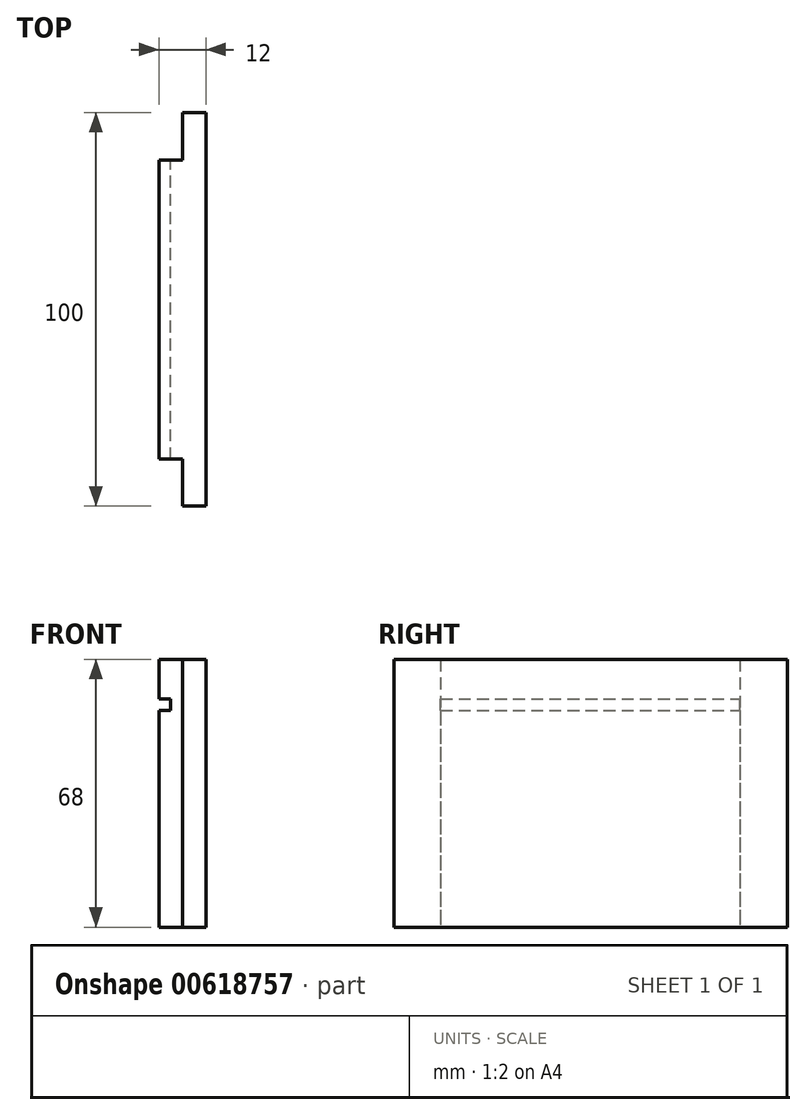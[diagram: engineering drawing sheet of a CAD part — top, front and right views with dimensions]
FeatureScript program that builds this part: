
annotation { "Feature Type Name" : "Feature", "Feature Type Description" : "" }
export const myFeature = defineFeature(function(context is Context, id is Id, definition is map)
    precondition{}
    {
        {
            var Q0;
            Q0=qCreatedBy(makeId("Front.planeOp"),FACE);
            var sketch = newSketch(context, id + "F0", { "sketchPlane" : qUnion([Q0])});
            skLineSegment(sketch, "E0.bottom", {"start": v(6, -34) * mm, "end": v(-6, -34) * mm});
            skLineSegment(sketch, "E0.top", {"start": v(6, 34) * mm, "end": v(-6, 34) * mm});
            skLineSegment(sketch, "E0.left", {"start": v(6, -34) * mm, "end": v(6, 34) * mm});
            skLineSegment(sketch, "E0.right", {"start": v(-6, -34) * mm, "end": v(-6, 21) * mm});
            skPoint(sketch, "E0.middle", {"position": v(0, 0) * mm});
            skLineSegment(sketch, "E1", {"start": v(-6, 34) * mm, "end": v(-6, 24) * mm});
            skLineSegment(sketch, "E2", {"start": v(-6, 24) * mm, "end": v(-3, 24) * mm});
            skLineSegment(sketch, "E3", {"start": v(-3, 24) * mm, "end": v(-3, 21) * mm});
            skLineSegment(sketch, "E4", {"start": v(-3, 21) * mm, "end": v(-6, 21) * mm});
            skLineSegment(sketch, "E5.trimOffspring", {"start": v(-6, 24) * mm, "end": v(-6, 34) * mm});
            skSolve(sketch);
        }
        {
            var Q0;
            Q0=makeQuery(id+"F0.imprint","IMPRINT",FACE,{"disambiguationData":[TD([[makeQuery(id+"F0.imprint","IMPRINT",EDGE,{"derivedFrom":sQuery(id+"F0.wireOp",EDGE,"E0.bottom")}),-1.0]])]});
            extrude(context, id + "F1", {"entities" : qUnion([Q0]), "depth" : 100 * mm, "offsetDistance" : 25 * mm});
        }
        {
            var Q0;
            Q0=makeQuery(id+"F1.opExtrude","SWEPT_FACE",FACE,{"disambiguationData":[OSD([sQuery(id+"F0.wireOp",EDGE,"E0.right")])]});
            var sketch = newSketch(context, id + "F2", { "sketchPlane" : qUnion([Q0])});
            skLineSegment(sketch, "E6", {"start": v(100.13, 34.18) * mm, "end": v(88.13, 34.18) * mm});
            skLineSegment(sketch, "E7.bottom", {"start": v(100.13, 34.18) * mm, "end": v(88.1, 34.18) * mm});
            skLineSegment(sketch, "E7.top", {"start": v(100.13, -34) * mm, "end": v(88.1, -34) * mm});
            skLineSegment(sketch, "E7.left", {"start": v(100.13, 34.18) * mm, "end": v(100.13, -34) * mm});
            skLineSegment(sketch, "E7.right", {"start": v(88.1, 34.18) * mm, "end": v(88.1, -34) * mm});
            skSolve(sketch);
        }
        {
            var Q0;
            Q0 = qSketchRegion(id + "F2", true);
            extrude(context, id + "F3", {"entities" : qUnion([Q0]), "operationType" : NewBodyOperationType.REMOVE, "oppositeDirection" : true, "depth" : 6 * mm, "offsetDistance" : 25 * mm});
        }
        {
            var Q0;
            Q0=makeQuery(id+"F1.opExtrude","SWEPT_FACE",FACE,{"disambiguationData":[OSD([sQuery(id+"F0.wireOp",EDGE,"E0.right")])]});
            var sketch = newSketch(context, id + "F4", { "sketchPlane" : qUnion([Q0])});
            skLineSegment(sketch, "E8", {"start": v(0.81, 34.18) * mm, "end": v(12.81, 34.18) * mm});
            skLineSegment(sketch, "E9.bottom", {"start": v(0, 34.18) * mm, "end": v(12.06, 34.18) * mm});
            skLineSegment(sketch, "E9.top", {"start": v(0, -34) * mm, "end": v(12.06, -34) * mm});
            skLineSegment(sketch, "E9.left", {"start": v(0, 34.18) * mm, "end": v(0, -34) * mm});
            skLineSegment(sketch, "E9.right", {"start": v(12.06, 34.18) * mm, "end": v(12.06, -34) * mm});
            skSolve(sketch);
        }
        {
            var Q0;
            Q0 = qSketchRegion(id + "F4", true);
            extrude(context, id + "F5", {"entities" : qUnion([Q0]), "operationType" : NewBodyOperationType.REMOVE, "oppositeDirection" : true, "depth" : 6 * mm, "offsetDistance" : 25 * mm});
        }
    });
